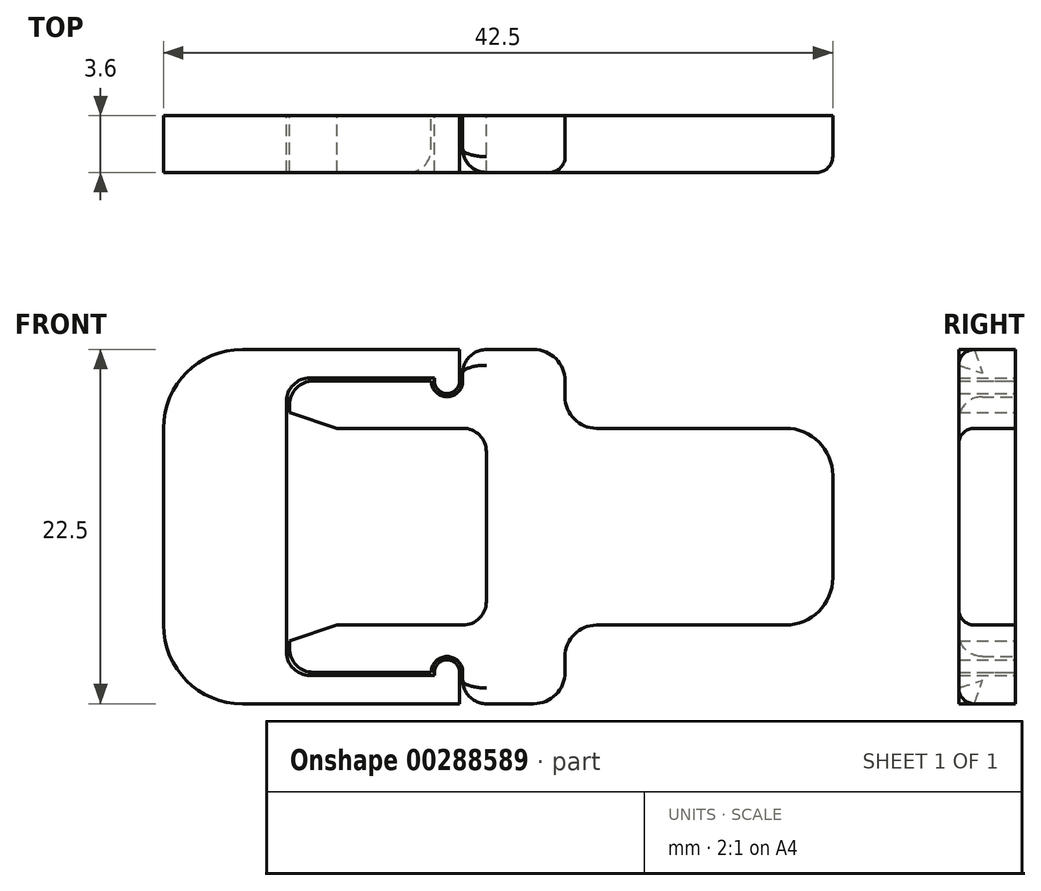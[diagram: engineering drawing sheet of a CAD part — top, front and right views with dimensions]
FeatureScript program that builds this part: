
annotation { "Feature Type Name" : "Feature", "Feature Type Description" : "" }
export const myFeature = defineFeature(function(context is Context, id is Id, definition is map)
    precondition{}
    {
        {
            var Q0;
            Q0=qCreatedBy(makeId("Front.planeOp"),FACE);
            var sketch = newSketch(context, id + "F0", { "sketchPlane" : qUnion([Q0])});
            skLineSegment(sketch, "E0.bottom", {"start": v(4.75, 6.25) * mm, "end": v(-3.25, 6.25) * mm});
            skLineSegment(sketch, "E0.top", {"start": v(4.75, -6.25) * mm, "end": v(-3.25, -6.25) * mm});
            skLineSegment(sketch, "E0.left", {"start": v(6.25, 4.75) * mm, "end": v(6.25, -4.75) * mm});
            skLineSegment(sketch, "E0.right", {"start": v(-6.25, 6.25) * mm, "end": v(-6.25, -6.25) * mm, "construction": true});
            skPoint(sketch, "E0.middle", {"position": v(0, 0) * mm});
            skPoint(sketch, "E1.visualSharp", {"position": v(6.25, 6.25) * mm});
            skArc(sketch, "E1.filletArc", {"start": v(6.25, 4.75) * mm, "mid": v(5.81, 5.81) * mm, "end": v(4.75, 6.25) * mm});
            skPoint(sketch, "E2.visualSharp", {"position": v(6.25, -6.25) * mm});
            skArc(sketch, "E2.filletArc", {"start": v(4.75, -6.25) * mm, "mid": v(5.81, -5.81) * mm, "end": v(6.25, -4.75) * mm});
            skLineSegment(sketch, "E3.bottom", {"start": v(4.75, -11.25) * mm, "end": v(9.25, -11.25) * mm});
            skLineSegment(sketch, "E3.top", {"start": v(4.75, 11.25) * mm, "end": v(9.25, 11.25) * mm});
            skLineSegment(sketch, "E3.right", {"start": v(28.25, -3.25) * mm, "end": v(28.25, 3.25) * mm});
            skPoint(sketch, "E4.visualSharp", {"position": v(28.25, 11.25) * mm});
            skPoint(sketch, "E5.visualSharp", {"position": v(28.25, -11.25) * mm});
            skLineSegment(sketch, "E6", {"start": v(0, 0) * mm, "end": v(-25.44, 0) * mm, "construction": true});
            skLineSegment(sketch, "E7", {"start": v(-3.25, 6.25) * mm, "end": v(-6.25, 7.25) * mm});
            skLineSegment(sketch, "E8", {"start": v(-6.25, 7.25) * mm, "end": v(-6.25, 9.25) * mm});
            skLineSegment(sketch, "E9.MirrorCS", {"start": v(-3.25, -6.25) * mm, "end": v(-6.25, -7.25) * mm});
            skLineSegment(sketch, "E10.MirrorCS", {"start": v(-6.25, -7.25) * mm, "end": v(-6.25, -9.25) * mm});
            skLineSegment(sketch, "E11", {"start": v(-6.25, 9.25) * mm, "end": v(2.75, 9.25) * mm});
            skArc(sketch, "E12", {"start": v(2.75, 9.25) * mm, "mid": v(3.75, 8.25) * mm, "end": v(4.75, 9.25) * mm});
            skLineSegment(sketch, "E13", {"start": v(4.75, 9.25) * mm, "end": v(4.75, 11.25) * mm});
            skLineSegment(sketch, "E14.MirrorCS", {"start": v(-6.25, -9.25) * mm, "end": v(2.75, -9.25) * mm});
            skArc(sketch, "E15.MirrorCS", {"start": v(2.75, -9.25) * mm, "mid": v(3.75, -8.25) * mm, "end": v(4.75, -9.25) * mm});
            skLineSegment(sketch, "E16.MirrorCS", {"start": v(4.75, -9.25) * mm, "end": v(4.75, -11.25) * mm});
            skPoint(sketch, "E17.orphan", {"position": v(-6.25, 11.25) * mm});
            skPoint(sketch, "E18.orphan", {"position": v(-6.25, -11.25) * mm});
            skLineSegment(sketch, "E19", {"start": v(11.25, 9.25) * mm, "end": v(11.25, 8.25) * mm});
            skLineSegment(sketch, "E20", {"start": v(13.25, 6.25) * mm, "end": v(25.25, 6.25) * mm});
            skPoint(sketch, "E21.visualSharp", {"position": v(11.25, 6.25) * mm});
            skArc(sketch, "E21.filletArc", {"start": v(11.25, 8.25) * mm, "mid": v(11.84, 6.84) * mm, "end": v(13.25, 6.25) * mm});
            skPoint(sketch, "E22.visualSharp", {"position": v(11.25, 11.25) * mm});
            skArc(sketch, "E22.filletArc", {"start": v(11.25, 9.25) * mm, "mid": v(10.66, 10.66) * mm, "end": v(9.25, 11.25) * mm});
            skPoint(sketch, "E23.visualSharp", {"position": v(28.25, 6.25) * mm});
            skArc(sketch, "E23.filletArc", {"start": v(28.25, 3.25) * mm, "mid": v(27.37, 5.37) * mm, "end": v(25.25, 6.25) * mm});
            skArc(sketch, "E24.MirrorCS", {"start": v(11.25, -9.25) * mm, "mid": v(10.66, -10.66) * mm, "end": v(9.25, -11.25) * mm});
            skLineSegment(sketch, "E25.MirrorCS", {"start": v(11.25, -9.25) * mm, "end": v(11.25, -8.25) * mm});
            skArc(sketch, "E26.MirrorCS", {"start": v(11.25, -8.25) * mm, "mid": v(11.84, -6.84) * mm, "end": v(13.25, -6.25) * mm});
            skLineSegment(sketch, "E27.MirrorCS", {"start": v(13.25, -6.25) * mm, "end": v(25.25, -6.25) * mm});
            skArc(sketch, "E28.MirrorCS", {"start": v(28.25, -3.25) * mm, "mid": v(27.37, -5.37) * mm, "end": v(25.25, -6.25) * mm});
            skSolve(sketch);
        }
        {
            var Q0;
            Q0=makeQuery(id+"F0.imprint","IMPRINT",FACE,{"disambiguationData":[TD([[makeQuery(id+"F0.imprint","IMPRINT",EDGE,{"derivedFrom":sQuery(id+"F0.wireOp",EDGE,"E0.bottom")}),-1.0]])]});
            extrude(context, id + "F1", {"entities" : qUnion([Q0]), "endBound" : BoundingType.SYMMETRIC, "depth" : 3.6 * mm});
        }
        {
            var Q0;
            Q0=makeQuery(id+"F1.opExtrude","CAP_EDGE",EDGE,{"disambiguationData":[OSD([sQuery(id+"F0.wireOp",EDGE,"E3.right")])],"isStart":false});
            fillet(context, id + "F2", {"entities" : qUnion([Q0]), "radius" : 1 * mm, "tangentPropagation" : true, "allowEdgeOverflow" : false});
        }
        {
            var Q0;
            Q0=makeQuery(id+"F1.opExtrude","SWEPT_EDGE",EDGE,{"disambiguationData":[OSD([sQuery(id+"F0.wireOp",EDGE,"E8"),sQuery(id+"F0.wireOp",EDGE,"E11")])]});
            var Q1;
            Q1=makeQuery(id+"F1.opExtrude","SWEPT_EDGE",EDGE,{"disambiguationData":[OSD([sQuery(id+"F0.wireOp",EDGE,"E10.MirrorCS"),sQuery(id+"F0.wireOp",EDGE,"E14.MirrorCS")])]});
            var Q2;
            Q2=makeQuery(id+"F1.opExtrude","SWEPT_EDGE",EDGE,{"disambiguationData":[OSD([sQuery(id+"F0.wireOp",EDGE,"E3.bottom"),sQuery(id+"F0.wireOp",EDGE,"E16.MirrorCS")])]});
            var Q3;
            Q3=makeQuery(id+"F1.opExtrude","SWEPT_EDGE",EDGE,{"disambiguationData":[OSD([sQuery(id+"F0.wireOp",EDGE,"E3.top"),sQuery(id+"F0.wireOp",EDGE,"E13")])]});
            fillet(context, id + "F3", {"entities" : qUnion([Q0, Q1, Q2, Q3]), "radius" : 1.5 * mm, "tangentPropagation" : true, "allowEdgeOverflow" : false});
        }
        {
            var Q0;
            Q0=qCreatedBy(makeId("Front.planeOp"),FACE);
            var sketch = newSketch(context, id + "F4", { "sketchPlane" : qUnion([Q0])});
            skLineSegment(sketch, "E29.0", {"start": v(4.75, 6.25) * mm, "end": v(-3.25, 6.25) * mm, "construction": true});
            skLineSegment(sketch, "E29.1", {"start": v(4.75, -6.25) * mm, "end": v(-3.25, -6.25) * mm, "construction": true});
            skLineSegment(sketch, "E29.2", {"start": v(6.25, 4.75) * mm, "end": v(6.25, -4.75) * mm, "construction": true});
            skLineSegment(sketch, "E29.3", {"start": v(-6.25, 6.25) * mm, "end": v(-6.25, -6.25) * mm, "construction": true});
            skPoint(sketch, "E29.4", {"position": v(0, 0) * mm});
            skPoint(sketch, "E29.5", {"position": v(6.25, 6.25) * mm});
            skArc(sketch, "E29.6", {"start": v(6.25, 4.75) * mm, "mid": v(5.81, 5.81) * mm, "end": v(4.75, 6.25) * mm, "construction": true});
            skPoint(sketch, "E29.7", {"position": v(6.25, -6.25) * mm});
            skArc(sketch, "E29.8", {"start": v(4.75, -6.25) * mm, "mid": v(5.81, -5.81) * mm, "end": v(6.25, -4.75) * mm, "construction": true});
            skLineSegment(sketch, "E29.9", {"start": v(4.75, -11.25) * mm, "end": v(9.25, -11.25) * mm, "construction": true});
            skLineSegment(sketch, "E29.10", {"start": v(4.75, 11.25) * mm, "end": v(9.25, 11.25) * mm, "construction": true});
            skLineSegment(sketch, "E29.11", {"start": v(28.25, -3.25) * mm, "end": v(28.25, 3.25) * mm, "construction": true});
            skPoint(sketch, "E29.12", {"position": v(28.25, 11.25) * mm});
            skArc(sketch, "E29.13", {"start": v(48, 13) * mm, "mid": v(46.54, 16.54) * mm, "end": v(43, 18) * mm, "construction": true});
            skPoint(sketch, "E29.14", {"position": v(28.25, -11.25) * mm});
            skArc(sketch, "E29.15", {"start": v(43, -18) * mm, "mid": v(46.54, -16.54) * mm, "end": v(48, -13) * mm, "construction": true});
            skLineSegment(sketch, "E29.16", {"start": v(0, 0) * mm, "end": v(-25.44, 0) * mm, "construction": true});
            skLineSegment(sketch, "E29.17", {"start": v(-3.25, 6.25) * mm, "end": v(-6.25, 7.25) * mm, "construction": true});
            skLineSegment(sketch, "E29.18", {"start": v(-6.25, 7.25) * mm, "end": v(-6.25, 9.25) * mm, "construction": true});
            skLineSegment(sketch, "E29.19", {"start": v(-3.25, -6.25) * mm, "end": v(-6.25, -7.25) * mm, "construction": true});
            skLineSegment(sketch, "E29.20", {"start": v(-6.25, -7.25) * mm, "end": v(-6.25, -9.25) * mm, "construction": true});
            skLineSegment(sketch, "E29.21", {"start": v(-6.25, 9.25) * mm, "end": v(2.75, 9.25) * mm, "construction": true});
            skArc(sketch, "E29.22", {"start": v(2.75, 9.25) * mm, "mid": v(3.75, 8.25) * mm, "end": v(4.75, 9.25) * mm, "construction": true});
            skLineSegment(sketch, "E29.23", {"start": v(4.75, 9.25) * mm, "end": v(4.75, 11.25) * mm, "construction": true});
            skLineSegment(sketch, "E29.24", {"start": v(-6.25, -9.25) * mm, "end": v(2.75, -9.25) * mm, "construction": true});
            skArc(sketch, "E29.25", {"start": v(2.75, -9.25) * mm, "mid": v(3.75, -8.25) * mm, "end": v(4.75, -9.25) * mm, "construction": true});
            skLineSegment(sketch, "E29.26", {"start": v(4.75, -9.25) * mm, "end": v(4.75, -11.25) * mm, "construction": true});
            skPoint(sketch, "E29.28", {"position": v(-6.25, -11.25) * mm});
            skLineSegment(sketch, "E30", {"start": v(-14.25, 6.25) * mm, "end": v(-14.25, 0) * mm});
            skLineSegment(sketch, "E31", {"start": v(-9.25, 11.25) * mm, "end": v(4.55, 11.25) * mm});
            skLineSegment(sketch, "E32", {"start": v(4.55, 11.25) * mm, "end": v(4.55, 9.25) * mm});
            skLineSegment(sketch, "E33", {"start": v(-4.95, 9.45) * mm, "end": v(2.95, 9.45) * mm});
            skArc(sketch, "E34", {"start": v(2.95, 9.25) * mm, "mid": v(3.75, 8.45) * mm, "end": v(4.55, 9.25) * mm});
            skLineSegment(sketch, "E35", {"start": v(2.95, 9.25) * mm, "end": v(2.95, 9.45) * mm});
            skLineSegment(sketch, "E36", {"start": v(-6.45, 7.95) * mm, "end": v(-6.45, 0) * mm});
            skPoint(sketch, "E37.visualSharp", {"position": v(-6.45, 9.45) * mm});
            skArc(sketch, "E37.filletArc", {"start": v(-4.95, 9.45) * mm, "mid": v(-6.01, 9.01) * mm, "end": v(-6.45, 7.95) * mm});
            skPoint(sketch, "E38.visualSharp", {"position": v(-14.25, 11.25) * mm});
            skArc(sketch, "E38.filletArc", {"start": v(-9.25, 11.25) * mm, "mid": v(-12.79, 9.79) * mm, "end": v(-14.25, 6.25) * mm});
            skLineSegment(sketch, "E39.MirrorCS", {"start": v(-14.25, -6.25) * mm, "end": v(-14.25, 0) * mm});
            skArc(sketch, "E40.MirrorCS", {"start": v(-9.25, -11.25) * mm, "mid": v(-12.79, -9.79) * mm, "end": v(-14.25, -6.25) * mm});
            skLineSegment(sketch, "E41.MirrorCS", {"start": v(-9.25, -11.25) * mm, "end": v(4.55, -11.25) * mm});
            skLineSegment(sketch, "E42.MirrorCS", {"start": v(4.55, -11.25) * mm, "end": v(4.55, -9.25) * mm});
            skArc(sketch, "E43.MirrorCS", {"start": v(2.95, -9.25) * mm, "mid": v(3.75, -8.45) * mm, "end": v(4.55, -9.25) * mm});
            skLineSegment(sketch, "E44.MirrorCS", {"start": v(2.95, -9.25) * mm, "end": v(2.95, -9.45) * mm});
            skLineSegment(sketch, "E45.MirrorCS", {"start": v(-4.95, -9.45) * mm, "end": v(2.95, -9.45) * mm});
            skArc(sketch, "E46.MirrorCS", {"start": v(-4.95, -9.45) * mm, "mid": v(-6.01, -9.01) * mm, "end": v(-6.45, -7.95) * mm});
            skLineSegment(sketch, "E47.MirrorCS", {"start": v(-6.45, -7.95) * mm, "end": v(-6.45, 0) * mm});
            skSolve(sketch);
        }
        {
            var Q0;
            Q0 = qSketchRegion(id + "F4", true);
            extrude(context, id + "F5", {"entities" : qUnion([Q0]), "endBound" : BoundingType.SYMMETRIC, "depth" : 3.6 * mm});
        }
    });
